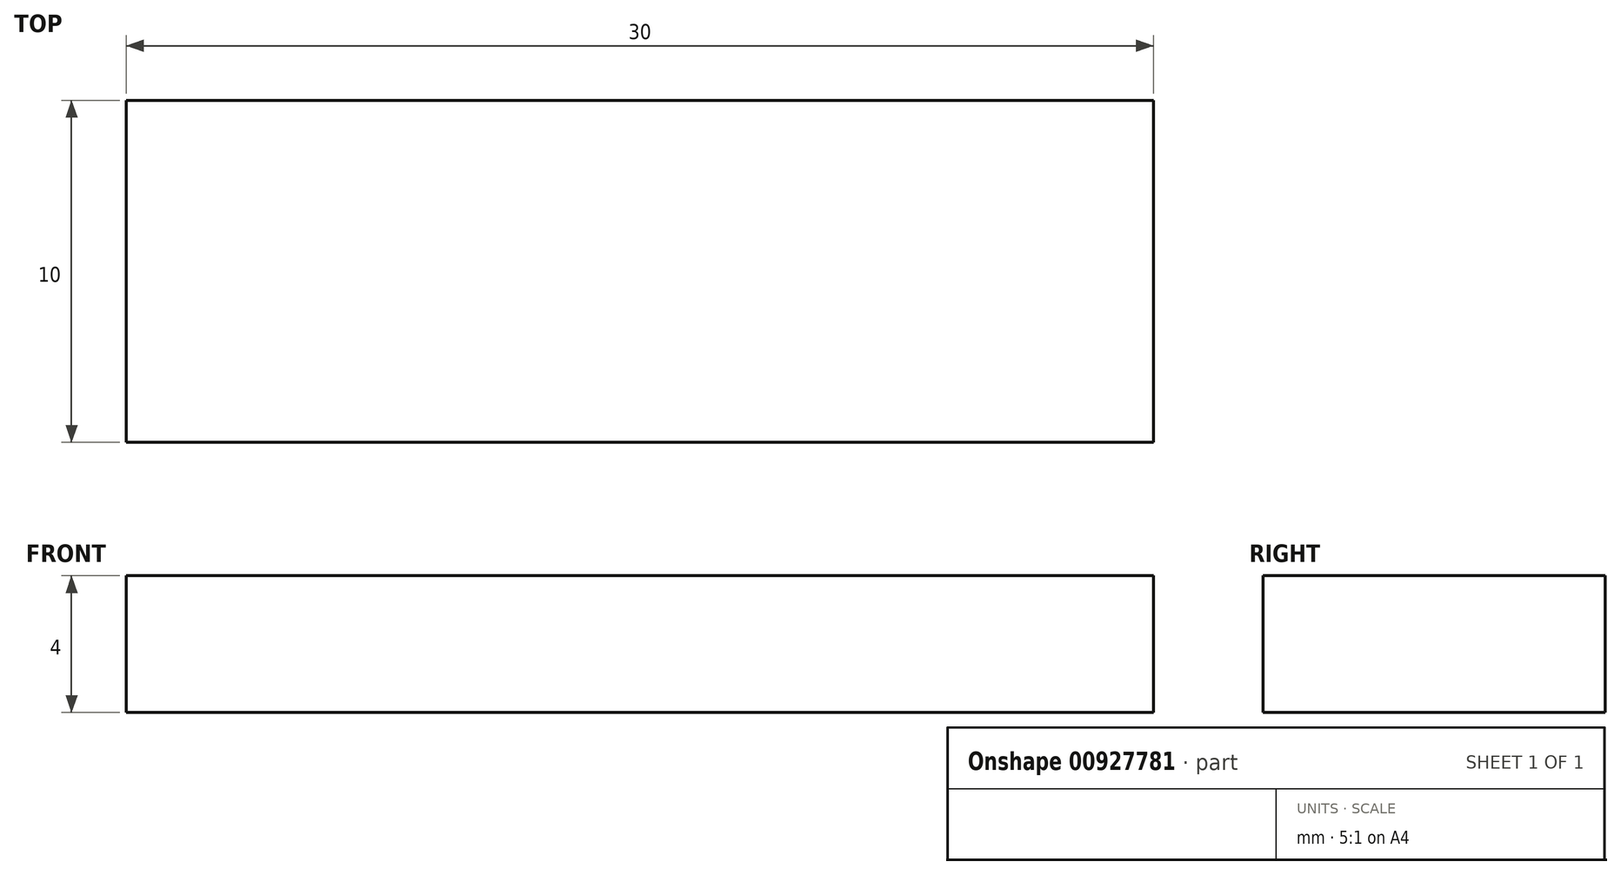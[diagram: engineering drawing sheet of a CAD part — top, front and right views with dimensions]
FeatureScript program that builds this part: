
annotation { "Feature Type Name" : "Feature", "Feature Type Description" : "" }
export const myFeature = defineFeature(function(context is Context, id is Id, definition is map)
    precondition{}
    {
        {
            var Q0;
            Q0=qCreatedBy(makeId("Top.planeOp"),FACE);
            var sketch = newSketch(context, id + "F0", { "sketchPlane" : qUnion([Q0])});
            skLineSegment(sketch, "E0.bottom", {"start": v(15, -5) * mm, "end": v(-15, -5) * mm});
            skLineSegment(sketch, "E0.top", {"start": v(15, 5) * mm, "end": v(-15, 5) * mm});
            skLineSegment(sketch, "E0.left", {"start": v(15, -5) * mm, "end": v(15, 5) * mm});
            skLineSegment(sketch, "E0.right", {"start": v(-15, -5) * mm, "end": v(-15, 5) * mm});
            skPoint(sketch, "E0.middle", {"position": v(0, 0) * mm});
            skSolve(sketch);
        }
        {
            var Q0;
            Q0=makeQuery(id+"F0.imprint","IMPRINT",FACE,{"disambiguationData":[TD([[makeQuery(id+"F0.imprint","IMPRINT",EDGE,{"derivedFrom":sQuery(id+"F0.wireOp",EDGE,"E0.bottom")}),-1.0]])]});
            extrude(context, id + "F1", {"entities" : qUnion([Q0]), "depth" : 4 * mm, "offsetDistance" : 25 * mm});
        }
    });
